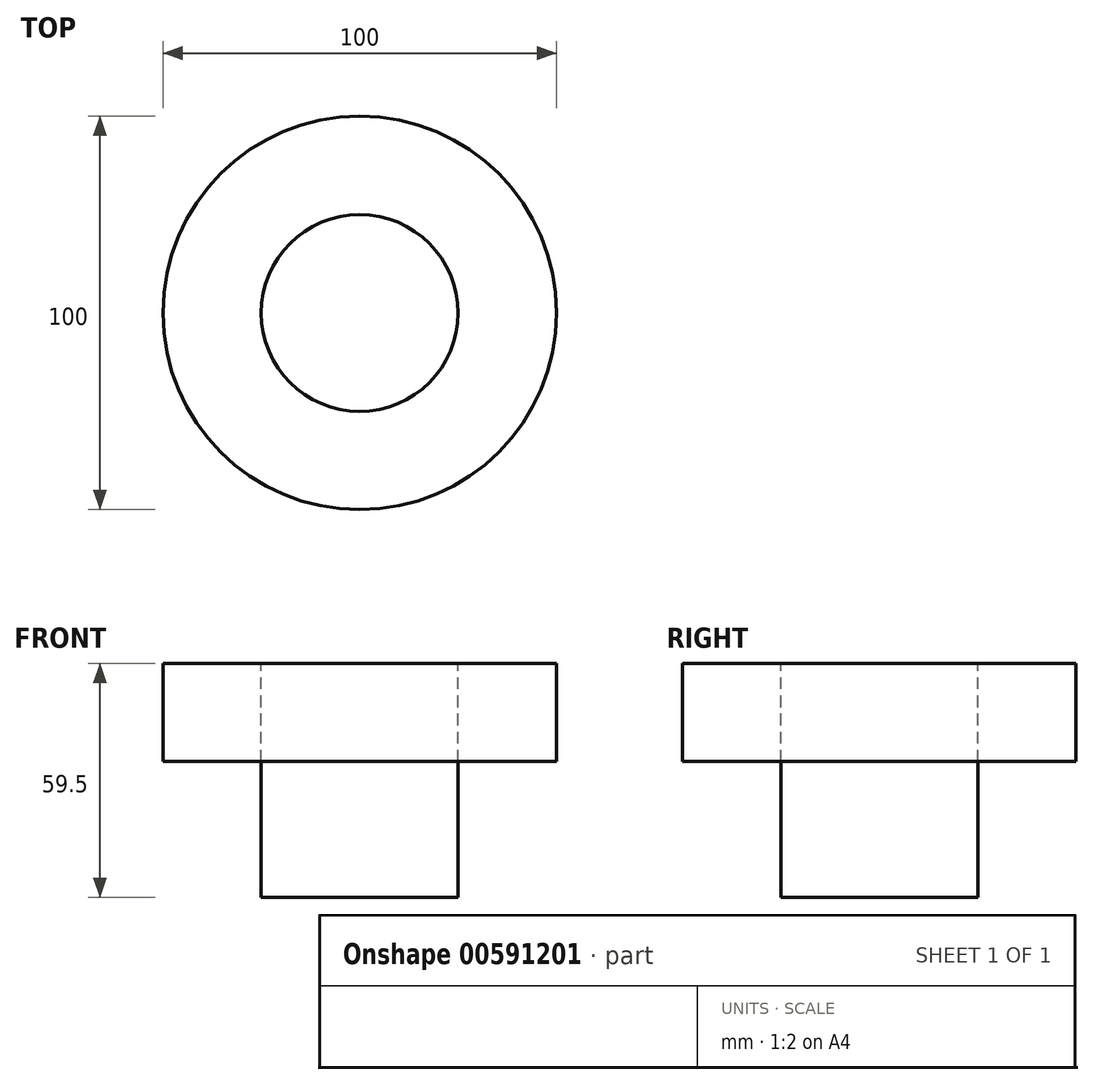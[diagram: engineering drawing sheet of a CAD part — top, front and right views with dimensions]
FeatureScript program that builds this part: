
annotation { "Feature Type Name" : "Feature", "Feature Type Description" : "" }
export const myFeature = defineFeature(function(context is Context, id is Id, definition is map)
    precondition{}
    {
        {
            var Q0;
            Q0=qCreatedBy(makeId("Top.planeOp"),FACE);
            var sketch = newSketch(context, id + "F0", { "sketchPlane" : qUnion([Q0])});
            skCircle(sketch, "E0", {"center": v(0, 0) * mm, "radius": 50 * mm});
            skSolve(sketch);
        }
        {
            var Q0;
            Q0 = qSketchRegion(id + "F0", true);
            extrude(context, id + "F1", {"entities" : qUnion([Q0]), "depth" : 25 * mm, "offsetDistance" : 25 * mm});
        }
        {
            var Q0;
            Q0=makeQuery(id+"F1.opExtrude","CAP_FACE",FACE,{"disambiguationData":[OSD([sQuery(id+"F0.wireOp",EDGE,"E0")])],"isStart":false});
            var sketch = newSketch(context, id + "F2", { "sketchPlane" : qUnion([Q0])});
            skCircle(sketch, "E1", {"center": v(0, 0) * mm, "radius": 25 * mm});
            skSolve(sketch);
        }
        {
            var Q0;
            Q0=makeQuery(id+"F2.imprint","IMPRINT",FACE,{"disambiguationData":[TD([[makeQuery(id+"F2.imprint","IMPRINT",EDGE,{"derivedFrom":sQuery(id+"F2.wireOp",EDGE,"E1")}),1.0]])]});
            extrude(context, id + "F3", {"entities" : qUnion([Q0]), "oppositeDirection" : true, "depth" : 59.5 * mm, "offsetDistance" : 25 * mm});
        }
    });
